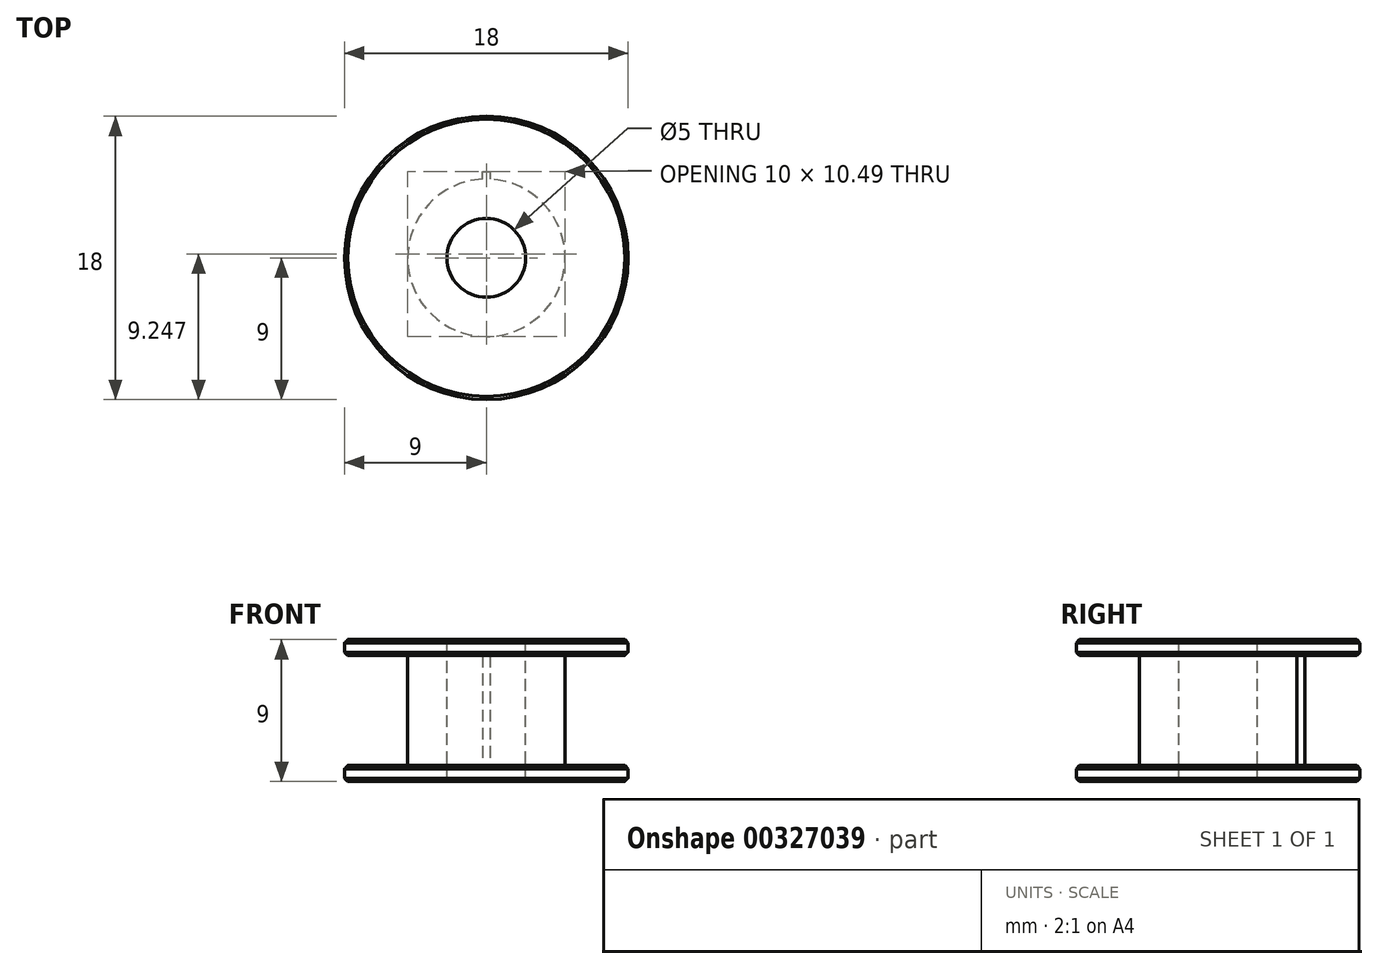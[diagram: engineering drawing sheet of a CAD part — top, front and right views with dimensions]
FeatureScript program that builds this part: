
annotation { "Feature Type Name" : "Feature", "Feature Type Description" : "" }
export const myFeature = defineFeature(function(context is Context, id is Id, definition is map)
    precondition{}
    {
        {
            var Q0;
            Q0=qCreatedBy(makeId("Front.planeOp"),FACE);
            var sketch = newSketch(context, id + "F0", { "sketchPlane" : qUnion([Q0])});
            skLineSegment(sketch, "E0", {"start": v(0, 0) * mm, "end": v(9, 0) * mm});
            skLineSegment(sketch, "E1", {"start": v(9, 0) * mm, "end": v(9, 1) * mm});
            skLineSegment(sketch, "E2", {"start": v(9, 1) * mm, "end": v(5, 1) * mm});
            skLineSegment(sketch, "E3", {"start": v(5, 1) * mm, "end": v(5, 8) * mm});
            skLineSegment(sketch, "E4", {"start": v(5, 8) * mm, "end": v(9, 8) * mm});
            skLineSegment(sketch, "E5", {"start": v(9, 8) * mm, "end": v(9, 9) * mm});
            skLineSegment(sketch, "E6", {"start": v(9, 9) * mm, "end": v(0, 9) * mm});
            skLineSegment(sketch, "E7", {"start": v(0, 9) * mm, "end": v(0, 0) * mm, "construction": true});
            skLineSegment(sketch, "E8", {"start": v(2.5, 9) * mm, "end": v(2.5, 0) * mm});
            skSolve(sketch);
        }
        {
            var Q0;
            {var subQ0=sQuery(id+"F0.wireOp",EDGE,"E1");Q0=makeQuery(id+"F0.imprint","IMPRINT",FACE,{"disambiguationData":[TD([[makeQuery(id+"F0.imprint","IMPRINT",EDGE,{"derivedFrom":subQ0}),1.0]])]});}
            var Q1;
            Q1=sQuery(id+"F0.wireOp",EDGE,"E7");
            revolve(context, id + "F1", {"entities" : qUnion([Q0]), "axis" : qUnion([Q1]), "revolveType" : RevolveType.FULL});
        }
        {
            var Q0;
            Q0=makeQuery(id+"F1.opRevolve","SWEPT_FACE",FACE,{"disambiguationData":[OSD([sQuery(id+"F0.wireOp",EDGE,"E2")])]});
            var sketch = newSketch(context, id + "F2", { "sketchPlane" : qUnion([Q0])});
            skLineSegment(sketch, "E9", {"start": v(-0.25, 5) * mm, "end": v(-0.25, 5.5) * mm});
            skLineSegment(sketch, "E10", {"start": v(-0.25, 5.5) * mm, "end": v(0.25, 5.5) * mm});
            skLineSegment(sketch, "E11", {"start": v(0.25, 5.5) * mm, "end": v(0.25, 5) * mm});
            skLineSegment(sketch, "E12", {"start": v(0, 5.5) * mm, "end": v(0, 0) * mm, "construction": true});
            skSolve(sketch);
        }
        {
            var Q0;
            {var subQ0=sQuery(id+"F2.wireOp",EDGE,"E9");Q0=makeQuery(id+"F2.imprint","IMPRINT",FACE,{"disambiguationData":[TD([[makeQuery(id+"F2.imprint","IMPRINT",EDGE,{"derivedFrom":subQ0}),-1.0]])]});}
            var Q1;
            Q1=makeQuery(id+"F1.opRevolve","SWEPT_FACE",FACE,{"disambiguationData":[OSD([sQuery(id+"F0.wireOp",EDGE,"E4")])]});
            extrude(context, id + "F3", {"entities" : qUnion([Q0]), "operationType" : NewBodyOperationType.ADD, "endBound" : BoundingType.UP_TO_SURFACE, "endBoundEntityFace" : qUnion([Q1]), "depth" : 25 * mm});
        }
        {
            var Q0;
            Q0=makeQuery(id+"F1.opRevolve","SWEPT_EDGE",EDGE,{"disambiguationData":[OSD([sQuery(id+"F0.wireOp",EDGE,"E5"),sQuery(id+"F0.wireOp",EDGE,"E6")])]});
            var Q1;
            Q1=makeQuery(id+"F1.opRevolve","SWEPT_EDGE",EDGE,{"disambiguationData":[OSD([sQuery(id+"F0.wireOp",EDGE,"E4"),sQuery(id+"F0.wireOp",EDGE,"E5")])]});
            var Q2;
            Q2=makeQuery(id+"F1.opRevolve","SWEPT_EDGE",EDGE,{"disambiguationData":[OSD([sQuery(id+"F0.wireOp",EDGE,"E1"),sQuery(id+"F0.wireOp",EDGE,"E2")])]});
            var Q3;
            Q3=makeQuery(id+"F1.opRevolve","SWEPT_EDGE",EDGE,{"disambiguationData":[OSD([sQuery(id+"F0.wireOp",EDGE,"E0"),sQuery(id+"F0.wireOp",EDGE,"E1")])]});
            chamfer(context, id + "F4", {"entities" : qUnion([Q0, Q1, Q2, Q3]), "width" : 0.2 * mm, "tangentPropagation" : true});
        }
    });
